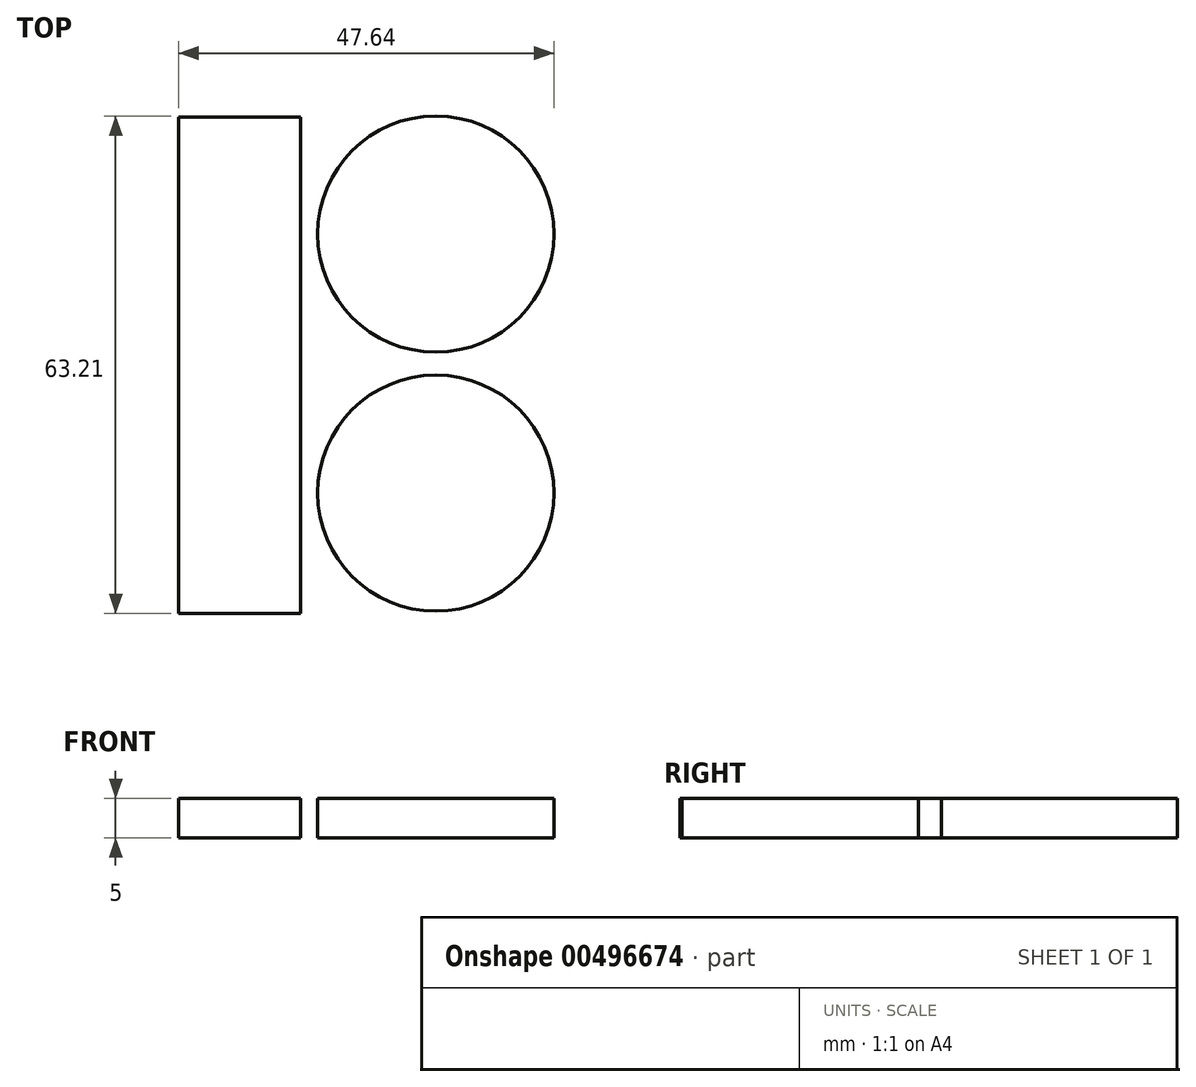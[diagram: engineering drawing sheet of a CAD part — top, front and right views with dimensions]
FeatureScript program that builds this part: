
annotation { "Feature Type Name" : "Feature", "Feature Type Description" : "" }
export const myFeature = defineFeature(function(context is Context, id is Id, definition is map)
    precondition{}
    {
        {
            var Q0;
            Q0=qCreatedBy(makeId("Top.planeOp"),FACE);
            var sketch = newSketch(context, id + "F0", { "sketchPlane" : qUnion([Q0])});
            skCircle(sketch, "E0", {"center": v(21.48, 29.88) * mm, "radius": 15 * mm});
            skCircle(sketch, "E1", {"center": v(21.48, -3.03) * mm, "radius": 15 * mm});
            skLineSegment(sketch, "E2", {"start": v(4.31, 44.75) * mm, "end": v(4.31, -18.33) * mm});
            skLineSegment(sketch, "E3", {"start": v(4.31, -18.33) * mm, "end": v(-11.16, -18.33) * mm});
            skLineSegment(sketch, "E4", {"start": v(-11.16, -18.33) * mm, "end": v(-11.16, 44.75) * mm});
            skLineSegment(sketch, "E5", {"start": v(-11.16, 44.75) * mm, "end": v(4.31, 44.75) * mm});
            skSolve(sketch);
        }
        {
            var Q0;
            Q0 = qSketchRegion(id + "F0", true);
            extrude(context, id + "F1", {"entities" : qUnion([Q0]), "depth" : 5 * mm, "offsetDistance" : 25 * mm});
        }
    });
